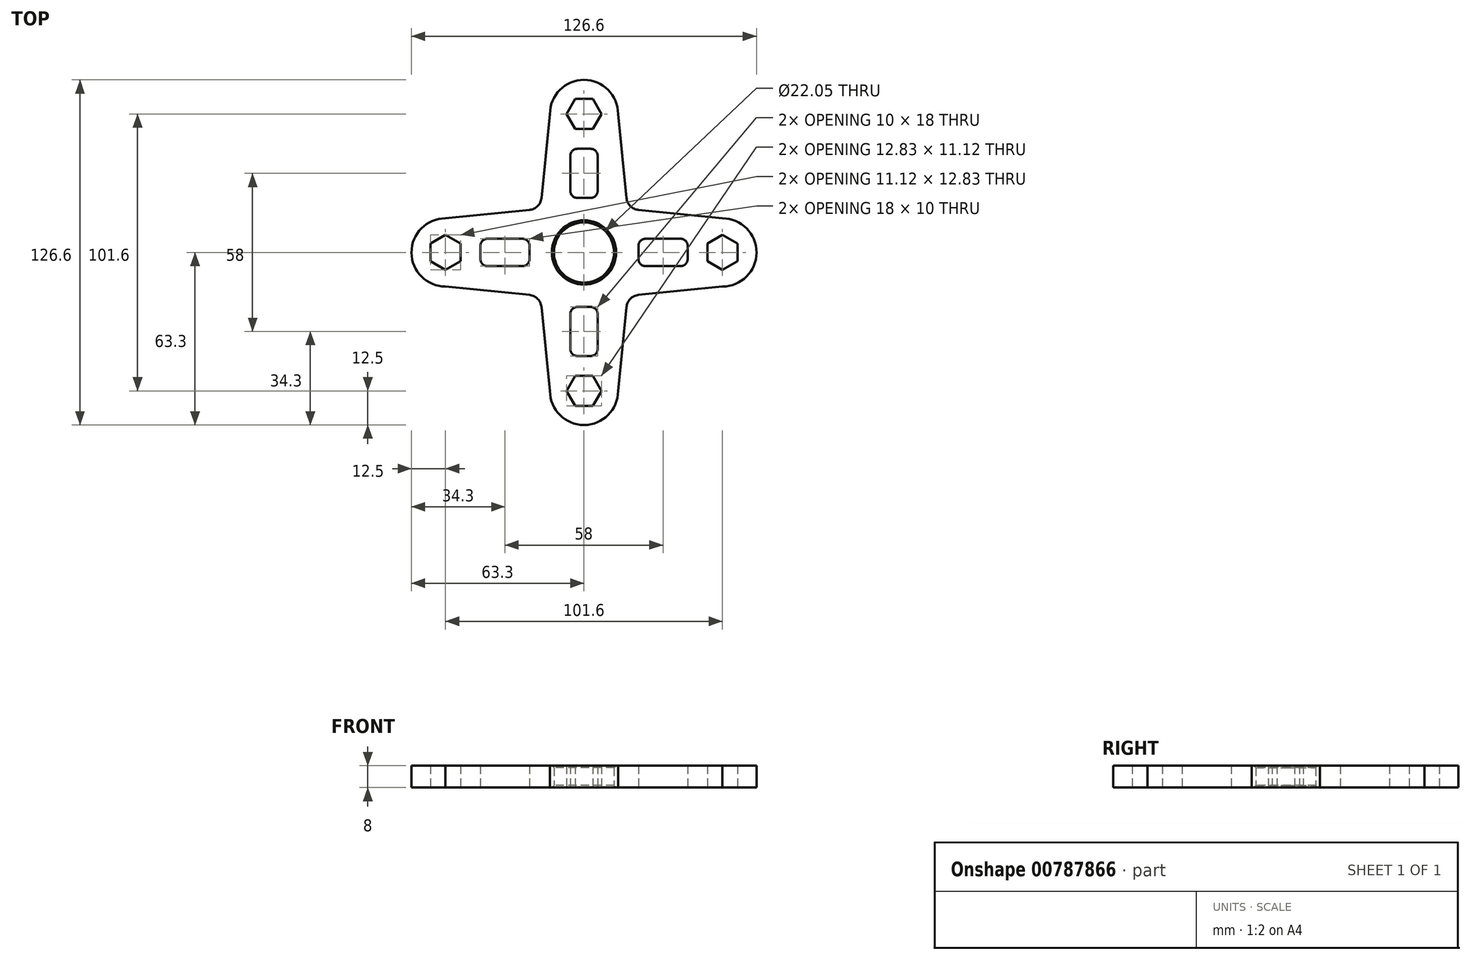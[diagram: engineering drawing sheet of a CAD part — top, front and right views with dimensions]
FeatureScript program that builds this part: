
annotation { "Feature Type Name" : "Feature", "Feature Type Description" : "" }
export const myFeature = defineFeature(function(context is Context, id is Id, definition is map)
    precondition{}
    {
        {
            var Q0;
            Q0=qCreatedBy(makeId("Top.planeOp"),FACE);
            var sketch = newSketch(context, id + "F0", { "sketchPlane" : qUnion([Q0])});
            skCircle(sketch, "E0", {"center": v(0, 0) * mm, "radius": 11.03 * mm});
            skLineSegment(sketch, "E1", {"start": v(0, 0) * mm, "end": v(0, 50.8) * mm});
            skCircle(sketch, "E2", {"center": v(0, 50.8) * mm, "radius": 12.5 * mm});
            skLineSegment(sketch, "E3", {"start": v(0, 50.8) * mm, "end": v(0, 63.3) * mm});
            skPoint(sketch, "E4", {"position": v(-12.5, 50.8) * mm});
            skPoint(sketch, "E5", {"position": v(12.5, 50.8) * mm});
            skLineSegment(sketch, "E6", {"start": v(-12.5, 50.8) * mm, "end": v(12.5, 50.8) * mm});
            skCircle(sketch, "E7", {"center": v(0, 0) * mm, "radius": 17.5 * mm});
            skLineSegment(sketch, "E8", {"start": v(-17.41, 1.74) * mm, "end": v(-12.5, 50.8) * mm});
            skLineSegment(sketch, "E9", {"start": v(12.5, 50.8) * mm, "end": v(17.41, 1.74) * mm});
            skPoint(sketch, "E10", {"position": v(0, 38.3) * mm});
            skPoint(sketch, "E11", {"position": v(0, 38) * mm});
            skPoint(sketch, "E12", {"position": v(0, 20) * mm});
            skPoint(sketch, "E13", {"position": v(-5, 38) * mm});
            skPoint(sketch, "E14", {"position": v(5, 38) * mm});
            skPoint(sketch, "E15", {"position": v(-5, 20) * mm});
            skPoint(sketch, "E16", {"position": v(5, 20) * mm});
            skLineSegment(sketch, "E17", {"start": v(-2.5, 38) * mm, "end": v(2.5, 38) * mm});
            skLineSegment(sketch, "E18", {"start": v(-2.5, 20) * mm, "end": v(2.5, 20) * mm});
            skLineSegment(sketch, "E19", {"start": v(-5, 35.5) * mm, "end": v(-5, 22.5) * mm});
            skLineSegment(sketch, "E20", {"start": v(5, 22.5) * mm, "end": v(5, 35.5) * mm});
            skArc(sketch, "E21.filletArc", {"start": v(-2.5, 38) * mm, "mid": v(-4.27, 37.27) * mm, "end": v(-5, 35.5) * mm});
            skArc(sketch, "E22.filletArc", {"start": v(5, 35.5) * mm, "mid": v(4.27, 37.27) * mm, "end": v(2.5, 38) * mm});
            skArc(sketch, "E23.filletArc", {"start": v(-5, 22.5) * mm, "mid": v(-4.27, 20.73) * mm, "end": v(-2.5, 20) * mm});
            skArc(sketch, "E24.filletArc", {"start": v(2.5, 20) * mm, "mid": v(4.27, 20.73) * mm, "end": v(5, 22.5) * mm});
            skCircle(sketch, "E25.cCircle", {"center": v(0, 50.8) * mm, "radius": 5.56 * mm, "construction": true});
            skLineSegment(sketch, "E25.0", {"start": v(3.2, 45.24) * mm, "end": v(-3.2, 45.24) * mm});
            skLineSegment(sketch, "E25.1", {"start": v(-3.2, 45.24) * mm, "end": v(-6.42, 50.8) * mm});
            skLineSegment(sketch, "E25.2", {"start": v(-6.42, 50.8) * mm, "end": v(-3.2, 56.36) * mm});
            skLineSegment(sketch, "E25.3", {"start": v(-3.2, 56.36) * mm, "end": v(3.2, 56.36) * mm});
            skLineSegment(sketch, "E25.4", {"start": v(3.2, 56.36) * mm, "end": v(6.42, 50.8) * mm});
            skLineSegment(sketch, "E25.5", {"start": v(6.42, 50.8) * mm, "end": v(3.2, 45.24) * mm});
            skPoint(sketch, "E25.0.midPoint", {"position": v(0, 45.24) * mm});
            skSolve(sketch);
        }
        {
            var Q0;
            {var subQ0=sQuery(id+"F0.wireOp",EDGE,"E3");var subQ1=sQuery(id+"F0.wireOp",EDGE,"E2");var subQ2=makeQuery(id+"F0.imprint","INTERSECT",VERTEX,{"derivedFrom":[subQ1,subQ0]});Q0=makeQuery(id+"F0.imprint","IMPRINT",FACE,{"disambiguationData":[TD([[makeQuery(id+"F0.imprint","IMPRINT",EDGE,{"disambiguationData":[TD([[subQ2,1.0]])],"derivedFrom":subQ0}),1.0]])]});}
            var Q1;
            {var subQ0=sQuery(id+"F0.wireOp",EDGE,"E3");var subQ1=sQuery(id+"F0.wireOp",EDGE,"E2");var subQ2=makeQuery(id+"F0.imprint","INTERSECT",VERTEX,{"derivedFrom":[subQ1,subQ0]});Q1=makeQuery(id+"F0.imprint","IMPRINT",FACE,{"disambiguationData":[TD([[makeQuery(id+"F0.imprint","IMPRINT",EDGE,{"disambiguationData":[TD([[subQ2,1.0]])],"derivedFrom":subQ0}),-1.0]])]});}
            var Q2;
            {var subQ0=sQuery(id+"F0.wireOp",EDGE,"E2");var subQ1=sQuery(id+"F0.wireOp",EDGE,"E1");var subQ2=makeQuery(id+"F0.imprint","INTERSECT",VERTEX,{"derivedFrom":[subQ1,subQ0]});Q2=makeQuery(id+"F0.imprint","IMPRINT",FACE,{"disambiguationData":[TD([[makeQuery(id+"F0.imprint","IMPRINT",EDGE,{"disambiguationData":[TD([[subQ2,-1.0]])],"derivedFrom":subQ1}),-1.0]])]});}
            var Q3;
            {var subQ0=sQuery(id+"F0.wireOp",EDGE,"E2");var subQ1=sQuery(id+"F0.wireOp",EDGE,"E1");var subQ2=makeQuery(id+"F0.imprint","INTERSECT",VERTEX,{"derivedFrom":[subQ1,subQ0]});Q3=makeQuery(id+"F0.imprint","IMPRINT",FACE,{"disambiguationData":[TD([[makeQuery(id+"F0.imprint","IMPRINT",EDGE,{"disambiguationData":[TD([[subQ2,-1.0]])],"derivedFrom":subQ1}),1.0]])]});}
            var Q4;
            {var subQ0=sQuery(id+"F0.wireOp",EDGE,"E8");Q4=makeQuery(id+"F0.imprint","IMPRINT",FACE,{"disambiguationData":[TD([[makeQuery(id+"F0.imprint","IMPRINT",EDGE,{"derivedFrom":subQ0}),-1.0]])]});}
            var Q5;
            {var subQ0=sQuery(id+"F0.wireOp",EDGE,"E9");Q5=makeQuery(id+"F0.imprint","IMPRINT",FACE,{"disambiguationData":[TD([[makeQuery(id+"F0.imprint","IMPRINT",EDGE,{"derivedFrom":subQ0}),-1.0]])]});}
            var Q6;
            Q6=makeQuery(id+"F0.imprint","IMPRINT",FACE,{"disambiguationData":[TD([[makeQuery(id+"F0.imprint","IMPRINT",EDGE,{"derivedFrom":sQuery(id+"F0.wireOp",EDGE,"E0")}),-1.0]])]});
            extrude(context, id + "F1", {"entities" : qUnion([Q0, Q1, Q2, Q3, Q4, Q5, Q6]), "depth" : 8 * mm, "offsetDistance" : 25 * mm});
        }
        {
            var Q0;
            Q0=qCreatedBy(makeId("Front.planeOp"),FACE);
            var sketch = newSketch(context, id + "F2", { "sketchPlane" : qUnion([Q0])});
            skLineSegment(sketch, "E26", {"start": v(0, 0) * mm, "end": v(0, 48.24) * mm});
            skSolve(sketch);
        }
        {
            var Q0;
            Q0=makeQuery(id+"F1.opExtrude","SWEPT_BODY",BODY,{"disambiguationData":[OSD([sQuery(id+"F0.wireOp",EDGE,"E0"),sQuery(id+"F0.wireOp",EDGE,"E2"),sQuery(id+"F0.wireOp",EDGE,"E7"),sQuery(id+"F0.wireOp",EDGE,"E8"),sQuery(id+"F0.wireOp",EDGE,"E9"),sQuery(id+"F0.wireOp",EDGE,"E17"),sQuery(id+"F0.wireOp",EDGE,"E18"),sQuery(id+"F0.wireOp",EDGE,"E19"),sQuery(id+"F0.wireOp",EDGE,"E20"),sQuery(id+"F0.wireOp",EDGE,"E21.filletArc"),sQuery(id+"F0.wireOp",EDGE,"E22.filletArc"),sQuery(id+"F0.wireOp",EDGE,"E23.filletArc"),sQuery(id+"F0.wireOp",EDGE,"E24.filletArc"),sQuery(id+"F0.wireOp",EDGE,"Os3FJgRO-5Fuf-hTji-JzkR-HfctrSJYmE6O")])]});
            var Q1;
            Q1=sQuery(id+"F2.wireOp",EDGE,"E26");
            circularPattern(context, id + "F3", {"operationType" : NewBodyOperationType.ADD, "entities" : qUnion([Q0]), "axis" : qUnion([Q1]), "angle" : 360 * degree, "instanceCount" : 4, "equalSpace" : true});
        }
        {
            var Q0;
            Q0=makeQuery(id+"F3.boolean.opBoolean","INTERSECT",EDGE,{"derivedFrom":[makeQuery(id+"F1.opExtrude","SWEPT_FACE",FACE,{"disambiguationData":[OSD([sQuery(id+"F0.wireOp",EDGE,"E9")])]}),makeQuery(id+"F3.opPattern","COPY",FACE,{"derivedFrom":makeQuery(id+"F1.opExtrude","SWEPT_FACE",FACE,{"disambiguationData":[OSD([sQuery(id+"F0.wireOp",EDGE,"E8")])]}),"instanceName":"3"})]});
            var Q1;
            Q1=makeQuery(id+"F3.boolean.opBoolean","INTERSECT",EDGE,{"derivedFrom":[makeQuery(id+"F1.opExtrude","SWEPT_FACE",FACE,{"disambiguationData":[OSD([sQuery(id+"F0.wireOp",EDGE,"E8")])]}),makeQuery(id+"F3.opPattern","COPY",FACE,{"derivedFrom":makeQuery(id+"F1.opExtrude","SWEPT_FACE",FACE,{"disambiguationData":[OSD([sQuery(id+"F0.wireOp",EDGE,"E9")])]}),"instanceName":"1"})]});
            var Q2;
            Q2=makeQuery(id+"F3.boolean.opBoolean","INTERSECT",EDGE,{"derivedFrom":[makeQuery(id+"F3.opPattern","COPY",FACE,{"derivedFrom":makeQuery(id+"F1.opExtrude","SWEPT_FACE",FACE,{"disambiguationData":[OSD([sQuery(id+"F0.wireOp",EDGE,"E8")])]}),"instanceName":"1"}),makeQuery(id+"F3.opPattern","COPY",FACE,{"derivedFrom":makeQuery(id+"F1.opExtrude","SWEPT_FACE",FACE,{"disambiguationData":[OSD([sQuery(id+"F0.wireOp",EDGE,"E9")])]}),"instanceName":"2"})]});
            var Q3;
            Q3=makeQuery(id+"F3.boolean.opBoolean","INTERSECT",EDGE,{"derivedFrom":[makeQuery(id+"F3.opPattern","COPY",FACE,{"derivedFrom":makeQuery(id+"F1.opExtrude","SWEPT_FACE",FACE,{"disambiguationData":[OSD([sQuery(id+"F0.wireOp",EDGE,"E8")])]}),"instanceName":"2"}),makeQuery(id+"F3.opPattern","COPY",FACE,{"derivedFrom":makeQuery(id+"F1.opExtrude","SWEPT_FACE",FACE,{"disambiguationData":[OSD([sQuery(id+"F0.wireOp",EDGE,"E9")])]}),"instanceName":"3"})]});
            fillet(context, id + "F4", {"entities" : qUnion([Q0, Q1, Q2, Q3]), "radius" : 5 * mm, "tangentPropagation" : true, "allowEdgeOverflow" : false});
        }
        {
            var Q0;
            Q0=makeQuery(id+"F1.opExtrude","CAP_EDGE",EDGE,{"disambiguationData":[OSD([sQuery(id+"F0.wireOp",EDGE,"E0")])],"isStart":false});
            var Q1;
            Q1=makeQuery(id+"F1.opExtrude","CAP_EDGE",EDGE,{"disambiguationData":[OSD([sQuery(id+"F0.wireOp",EDGE,"E0")])],"isStart":true});
            chamfer(context, id + "F5", {"entities" : qUnion([Q0, Q1]), "width" : 0.76 * mm, "tangentPropagation" : true});
        }
    });
